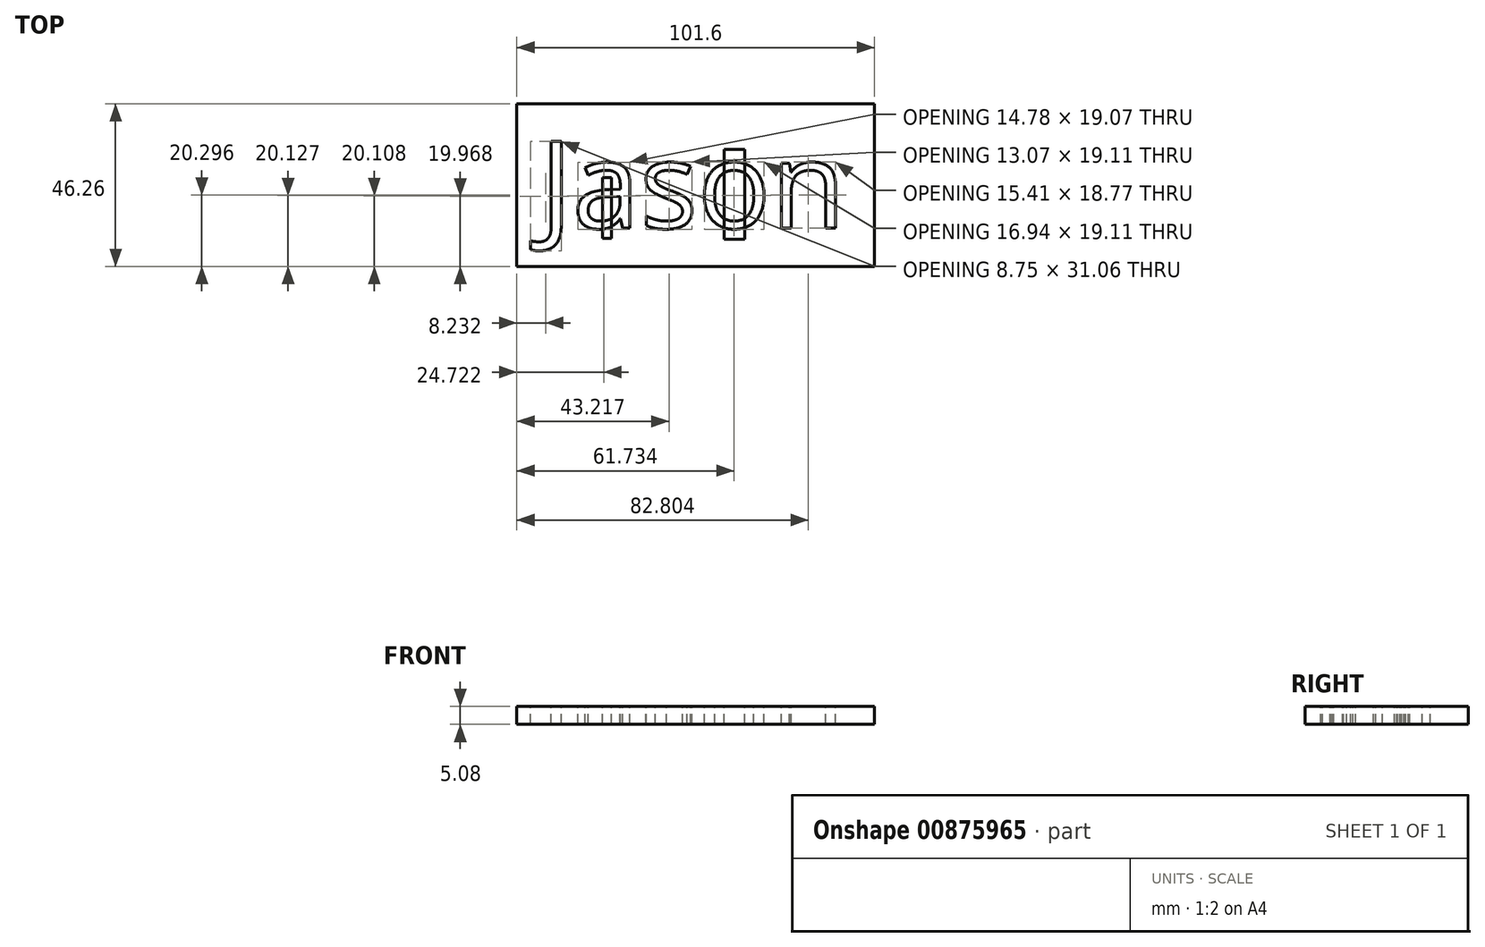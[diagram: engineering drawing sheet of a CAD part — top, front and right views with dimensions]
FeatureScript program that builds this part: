
annotation { "Feature Type Name" : "Feature", "Feature Type Description" : "" }
export const myFeature = defineFeature(function(context is Context, id is Id, definition is map)
    precondition{}
    {
        {
            var Q0;
            Q0=qCreatedBy(makeId("Top.planeOp"),FACE);
            var sketch = newSketch(context, id + "F0", { "sketchPlane" : qUnion([Q0])});
            skLineSegment(sketch, "E0.bottom", {"start": v(50.8, -23.13) * mm, "end": v(-50.8, -23.13) * mm});
            skLineSegment(sketch, "E0.top", {"start": v(50.8, 23.13) * mm, "end": v(-50.8, 23.13) * mm});
            skLineSegment(sketch, "E0.left", {"start": v(50.8, -23.13) * mm, "end": v(50.8, 23.13) * mm});
            skLineSegment(sketch, "E0.right", {"start": v(-50.8, -23.13) * mm, "end": v(-50.8, 23.13) * mm});
            skPoint(sketch, "E0.middle", {"position": v(0, 0) * mm});
            skSolve(sketch);
        }
        {
            var Q0;
            Q0=makeQuery(id+"F0.imprint","IMPRINT",FACE,{"disambiguationData":[TD([[makeQuery(id+"F0.imprint","IMPRINT",EDGE,{"derivedFrom":sQuery(id+"F0.wireOp",EDGE,"E0.bottom")}),-1.0]])]});
            extrude(context, id + "F1", {"entities" : qUnion([Q0]), "depth" : 5.08 * mm, "offsetDistance" : 25.4 * mm});
        }
        {
            var Q0;
            Q0=makeQuery(id+"F1.opExtrude","CAP_FACE",FACE,{"disambiguationData":[OSD([sQuery(id+"F0.wireOp",EDGE,"E0.bottom"),sQuery(id+"F0.wireOp",EDGE,"E0.top"),sQuery(id+"F0.wireOp",EDGE,"E0.left"),sQuery(id+"F0.wireOp",EDGE,"E0.right")])],"isStart":false});
            var sketch = newSketch(context, id + "F2", { "sketchPlane" : qUnion([Q0])});
            skText(sketch, "E1", { "text": "Jason", "fontName": "OpenSans-Regular.ttf"});
            const initialGuessF2  = {"E1": [-0.04425, -0.01222, 1, 0, 0.0248]};
            skSetInitialGuess(sketch, initialGuessF2);
            skSolve(sketch);
        }
        {
            var Q0;
            Q0 = qSketchRegion(id + "F2", true);
            extrude(context, id + "F3", {"entities" : qUnion([Q0]), "operationType" : NewBodyOperationType.REMOVE, "oppositeDirection" : true, "depth" : 25.4 * mm, "offsetDistance" : 25.4 * mm});
        }
        {
            var Q0;
            {var subQ0=sQuery(id+"F0.wireOp",EDGE,"E0.left");var subQ1=sQuery(id+"F0.wireOp",EDGE,"E0.bottom");var subQ2=sQuery(id+"F0.wireOp",EDGE,"E0.right");var subQ3=sQuery(id+"F0.wireOp",EDGE,"E0.top");Q0=makeQuery(id+"F3.boolean.opBoolean","SPLIT",FACE,{"disambiguationData":[TD([makeQuery(id+"F1.opExtrude","SWEPT_FACE",FACE,{"disambiguationData":[OSD([subQ1])]})])],"derivedFrom":makeQuery(id+"F1.opExtrude","CAP_FACE",FACE,{"disambiguationData":[OSD([subQ1,subQ3,subQ0,subQ2])],"isStart":false})});}
            var sketch = newSketch(context, id + "F4", { "sketchPlane" : qUnion([Q0])});
            skLineSegment(sketch, "E2.bottom", {"start": v(13.93, -15.38) * mm, "end": v(8.06, -15.38) * mm});
            skLineSegment(sketch, "E2.top", {"start": v(13.93, 10.08) * mm, "end": v(8.06, 10.08) * mm});
            skLineSegment(sketch, "E2.left", {"start": v(13.93, -15.38) * mm, "end": v(13.93, 10.08) * mm});
            skLineSegment(sketch, "E2.right", {"start": v(8.06, -15.38) * mm, "end": v(8.06, 10.08) * mm});
            skPoint(sketch, "E2.middle", {"position": v(11, -2.65) * mm});
            skLineSegment(sketch, "E3.bottom", {"start": v(-26.46, -15.1) * mm, "end": v(-23.85, -15.1) * mm});
            skLineSegment(sketch, "E3.top", {"start": v(-26.46, 2.16) * mm, "end": v(-23.85, 2.16) * mm});
            skLineSegment(sketch, "E3.left", {"start": v(-26.46, -15.1) * mm, "end": v(-26.46, 2.16) * mm});
            skLineSegment(sketch, "E3.right", {"start": v(-23.85, -15.1) * mm, "end": v(-23.85, 2.16) * mm});
            skPoint(sketch, "E3.middle", {"position": v(-25.15, -6.47) * mm});
            skSolve(sketch);
        }
        {
            var Q0;
            {var subQ0=makeQuery(id+"F3.boolean.opBoolean","COPY",EDGE,{"derivedFrom":makeQuery(id+"F3.opExtrude","CAP_EDGE",EDGE,{"disambiguationData":[OSD([sQuery(id+"F2.wireOp",EDGE,"E1.sketch_text.stroke-13")])],"isStart":true})});var subQ5=sQuery(id+"F4.wireOp",EDGE,"E3.left");var subQ6=makeQuery(id+"F4.imprint","INTERSECT",VERTEX,{"derivedFrom":[subQ0,subQ5]});Q0=makeQuery(id+"F4.imprint","IMPRINT",FACE,{"disambiguationData":[TD([[makeQuery(id+"F4.imprint","IMPRINT",EDGE,{"disambiguationData":[TD([[subQ6,-1.0]])],"derivedFrom":subQ5}),-1.0]])]});}
            var Q1;
            {var subQ1=sQuery(id+"F4.wireOp",EDGE,"E3.top");Q1=makeQuery(id+"F4.imprint","IMPRINT",FACE,{"disambiguationData":[TD([[makeQuery(id+"F4.imprint","IMPRINT",EDGE,{"derivedFrom":subQ1}),-1.0]])]});}
            var Q2;
            {var subQ1=sQuery(id+"F4.wireOp",EDGE,"E3.bottom");Q2=makeQuery(id+"F4.imprint","IMPRINT",FACE,{"disambiguationData":[TD([[makeQuery(id+"F4.imprint","IMPRINT",EDGE,{"derivedFrom":subQ1}),1.0]])]});}
            var Q3;
            {var subQ5=sQuery(id+"F4.wireOp",EDGE,"E2.top");Q3=makeQuery(id+"F4.imprint","IMPRINT",FACE,{"disambiguationData":[TD([[makeQuery(id+"F4.imprint","IMPRINT",EDGE,{"derivedFrom":subQ5}),1.0]])]});}
            var Q4;
            {var subQ1=makeQuery(id+"F3.boolean.opBoolean","COPY",EDGE,{"derivedFrom":makeQuery(id+"F3.opExtrude","CAP_EDGE",EDGE,{"disambiguationData":[OSD([sQuery(id+"F2.wireOp",EDGE,"E1.sketch_text.stroke-63")])],"isStart":true})});var subQ5=sQuery(id+"F4.wireOp",EDGE,"E2.left");var subQ6=makeQuery(id+"F4.imprint","INTERSECT",VERTEX,{"derivedFrom":[subQ1,subQ5]});Q4=makeQuery(id+"F4.imprint","IMPRINT",FACE,{"disambiguationData":[TD([[makeQuery(id+"F4.imprint","IMPRINT",EDGE,{"disambiguationData":[TD([[subQ6,-1.0]])],"derivedFrom":subQ5}),1.0]])]});}
            var Q5;
            {var subQ5=sQuery(id+"F4.wireOp",EDGE,"E2.bottom");Q5=makeQuery(id+"F4.imprint","IMPRINT",FACE,{"disambiguationData":[TD([[makeQuery(id+"F4.imprint","IMPRINT",EDGE,{"derivedFrom":subQ5}),-1.0]])]});}
            extrude(context, id + "F5", {"entities" : qUnion([Q0, Q1, Q2, Q3, Q4, Q5]), "oppositeDirection" : true, "depth" : 5.08 * mm, "offsetDistance" : 25.4 * mm});
        }
    });
